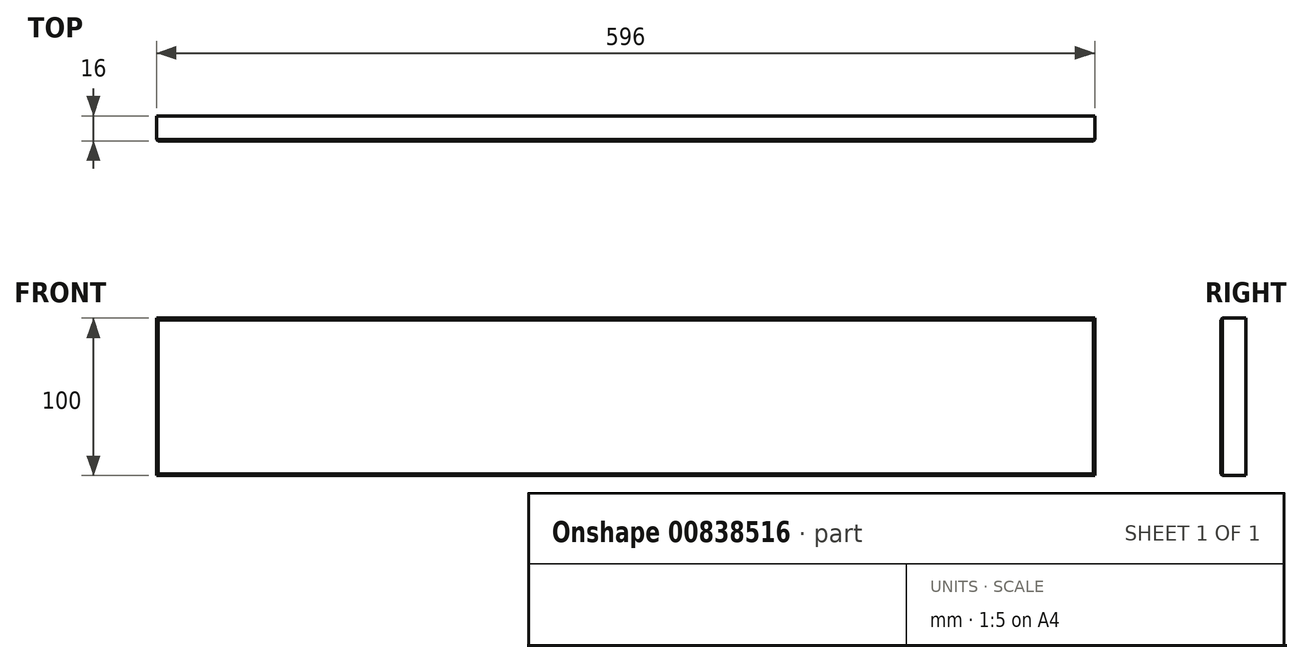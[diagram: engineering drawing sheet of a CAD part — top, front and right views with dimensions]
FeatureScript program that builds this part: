
annotation { "Feature Type Name" : "Feature", "Feature Type Description" : "" }
export const myFeature = defineFeature(function(context is Context, id is Id, definition is map)
    precondition{}
    {
        {
            var Q0;
            Q0=qCreatedBy(makeId("Front.planeOp"),FACE);
            var sketch = newSketch(context, id + "F0", { "sketchPlane" : qUnion([Q0])});
            skLineSegment(sketch, "E0.bottom", {"start": v(0, 0) * mm, "end": v(43.57, 0) * mm});
            skLineSegment(sketch, "E0.top", {"start": v(0, 38.66) * mm, "end": v(43.57, 38.66) * mm});
            skLineSegment(sketch, "E0.left", {"start": v(0, 0) * mm, "end": v(0, 38.66) * mm});
            skLineSegment(sketch, "E0.right", {"start": v(43.57, 0) * mm, "end": v(43.57, 38.66) * mm});
            skSolve(sketch);
        }
        {
            var Q0;
            Q0=makeQuery(id+"F0.imprint","IMPRINT",FACE,{"disambiguationData":[TD([[makeQuery(id+"F0.imprint","IMPRINT",EDGE,{"derivedFrom":sQuery(id+"F0.wireOp",EDGE,"E0.bottom")}),1.0]])]});
            extrude(context, id + "F1", {"entities" : qUnion([Q0]), "depth" : 16 * mm, "offsetDistance" : 25.4 * mm});
        }
        {
            var Q0;
            Q0=makeQuery(id+"F1.opExtrude","SWEPT_FACE",FACE,{"disambiguationData":[OSD([sQuery(id+"F0.wireOp",EDGE,"E0.left")])]});
            extrude(context, id + "F2", {"entities" : qUnion([Q0]), "operationType" : NewBodyOperationType.ADD, "oppositeDirection" : true, "depth" : 396 * mm, "offsetDistance" : 25 * mm});
        }
        {
            var Q0;
            {var subQ0=sQuery(id+"F0.wireOp",EDGE,"E0.bottom");Q0=makeQuery(id+"F2.boolean.opBoolean","MERGE",FACE,{"derivedFrom":[makeQuery(id+"F1.opExtrude","SWEPT_FACE",FACE,{"disambiguationData":[OSD([subQ0])]}),makeQuery(id+"F2.opExtrude","SWEPT_FACE",FACE,{"disambiguationData":[OSD([subQ0,sQuery(id+"F0.wireOp",EDGE,"E0.left")])]})]});}
            extrude(context, id + "F3", {"entities" : qUnion([Q0]), "operationType" : NewBodyOperationType.ADD, "oppositeDirection" : true, "depth" : 100 * mm, "offsetDistance" : 25 * mm});
        }
        {
            var Q0;
            {var subQ0=sQuery(id+"F0.wireOp",EDGE,"E0.left");var subQ1=sQuery(id+"F0.wireOp",EDGE,"E0.bottom");Q0=makeQuery(id+"F3.boolean.opBoolean","MERGE",FACE,{"derivedFrom":[makeQuery(id+"F2.opExtrude","CAP_FACE",FACE,{"disambiguationData":[OSD([subQ0])],"isStart":false}),makeQuery(id+"F3.opExtrude","SWEPT_FACE",FACE,{"disambiguationData":[OSD([subQ1,subQ0]),TDD([makeQuery(id+"F2.opExtrude","CAP_EDGE",EDGE,{"disambiguationData":[OSD([subQ1,subQ0])],"isStart":false})])]})]});}
            extrude(context, id + "F4", {"entities" : qUnion([Q0]), "operationType" : NewBodyOperationType.ADD, "depth" : 200 * mm, "offsetDistance" : 25 * mm});
        }
        {
            var Q0;
            {var subQ0=sQuery(id+"F0.wireOp",EDGE,"E0.left");var subQ1=sQuery(id+"F0.wireOp",EDGE,"E0.bottom");var subQ2=makeQuery(id+"F1.opExtrude","CAP_VERTEX",VERTEX,{"disambiguationData":[OSD([subQ1,subQ0])],"isStart":false});var subQ3=makeQuery(id+"F1.opExtrude","CAP_EDGE",EDGE,{"disambiguationData":[OSD([subQ0])],"isStart":false});Q0=makeQuery(id+"F4.boolean.opBoolean","MERGE",FACE,{"derivedFrom":[makeQuery(id+"F3.boolean.opBoolean","MERGE",FACE,{"derivedFrom":[makeQuery(id+"F2.boolean.opBoolean","MERGE",FACE,{"derivedFrom":[makeQuery(id+"F1.opExtrude","CAP_FACE",FACE,{"disambiguationData":[OSD([subQ1,sQuery(id+"F0.wireOp",EDGE,"E0.top"),subQ0,sQuery(id+"F0.wireOp",EDGE,"E0.right")])],"isStart":false}),makeQuery(id+"F2.opExtrude","SWEPT_FACE",FACE,{"disambiguationData":[OSD([subQ0]),TDD([subQ3])]})]}),makeQuery(id+"F3.opExtrude","SWEPT_FACE",FACE,{"disambiguationData":[OSD([subQ1,subQ0]),TDD([makeQuery(id+"F2.boolean.opBoolean","MERGE",EDGE,{"derivedFrom":[makeQuery(id+"F1.opExtrude","CAP_EDGE",EDGE,{"disambiguationData":[OSD([subQ1])],"isStart":false}),makeQuery(id+"F2.opExtrude","SWEPT_EDGE",EDGE,{"disambiguationData":[OSD([subQ1,subQ0]),TDD([subQ2])]})]})])]})]}),makeQuery(id+"F4.opExtrude","SWEPT_FACE",FACE,{"disambiguationData":[OSD([subQ1,subQ0]),TDD([makeQuery(id+"F3.boolean.opBoolean","MERGE",EDGE,{"derivedFrom":[makeQuery(id+"F2.opExtrude","CAP_EDGE",EDGE,{"disambiguationData":[OSD([subQ0]),TDD([subQ3])],"isStart":false}),makeQuery(id+"F3.opExtrude","SWEPT_EDGE",EDGE,{"disambiguationData":[OSD([subQ1,subQ0]),TDD([makeQuery(id+"F2.opExtrude","CAP_VERTEX",VERTEX,{"disambiguationData":[OSD([subQ1,subQ0]),TDD([subQ2])],"isStart":false})])]})]})])]})]});}
            chamfer(context, id + "F5", {"entities" : qUnion([Q0]), "width" : 1 * mm, "tangentPropagation" : true});
        }
    });
